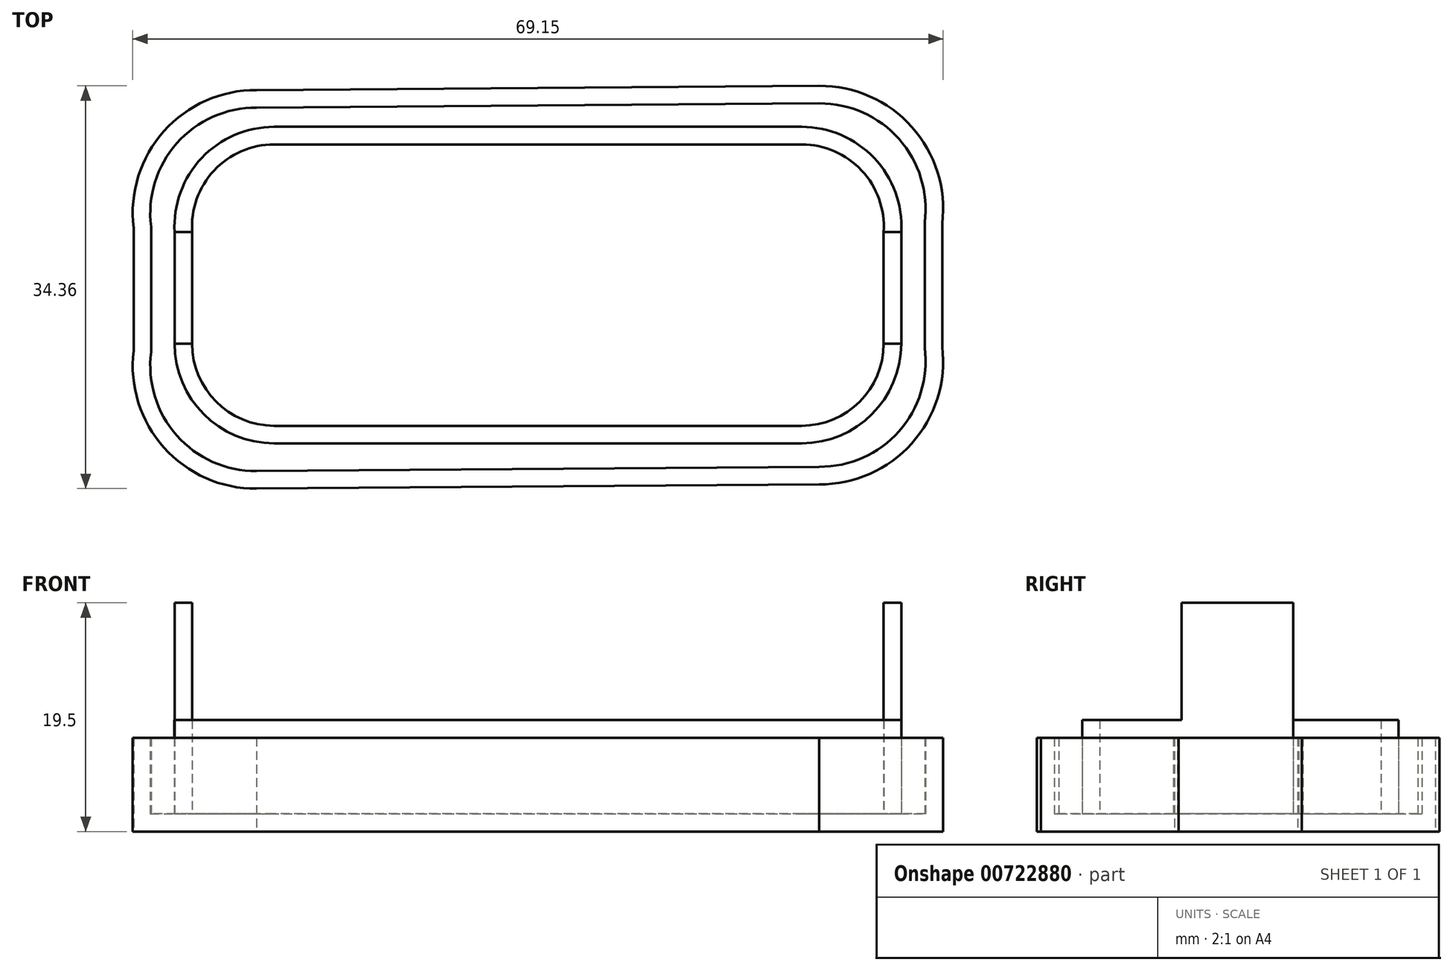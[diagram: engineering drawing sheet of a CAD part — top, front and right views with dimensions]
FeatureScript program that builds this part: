
annotation { "Feature Type Name" : "Feature", "Feature Type Description" : "" }
export const myFeature = defineFeature(function(context is Context, id is Id, definition is map)
    precondition{}
    {
        {
            var Q0;
            Q0=qCreatedBy(makeId("Top.planeOp"),FACE);
            var sketch = newSketch(context, id + "F0", { "sketchPlane" : qUnion([Q0])});
            skLineSegment(sketch, "E0.0", {"start": v(-24.12, -16.42) * mm, "end": v(23.88, -16.06) * mm});
            skArc(sketch, "E0.1", {"start": v(34.38, -4.31) * mm, "mid": v(31.79, -12.56) * mm, "end": v(23.88, -16.06) * mm});
            skLineSegment(sketch, "E0.2", {"start": v(34.38, 6.19) * mm, "end": v(34.38, -4.31) * mm});
            skArc(sketch, "E0.3", {"start": v(23.88, 17.94) * mm, "mid": v(31.79, 14.43) * mm, "end": v(34.38, 6.19) * mm});
            skLineSegment(sketch, "E0.4", {"start": v(-24.12, 17.58) * mm, "end": v(23.88, 17.94) * mm});
            skArc(sketch, "E0.5", {"start": v(-34.62, 5.83) * mm, "mid": v(-32.02, 14.07) * mm, "end": v(-24.12, 17.58) * mm});
            skLineSegment(sketch, "E0.6", {"start": v(-34.62, 5.83) * mm, "end": v(-34.62, -4.67) * mm});
            skArc(sketch, "E0.7", {"start": v(-24.12, -16.42) * mm, "mid": v(-32.02, -12.92) * mm, "end": v(-34.62, -4.67) * mm});
            skSolve(sketch);
        }
        {
            var Q0;
            Q0=qSketchRegion(id+"F0",true);
            extrude(context, id + "F1", {"entities" : qUnion([Q0]), "depth" : 8 * mm, "offsetDistance" : 25 * mm});
        }
        {
            var Q0;
            Q0=makeQuery(id+"F1.opExtrude","CAP_FACE",FACE,{"disambiguationData":[OSD([sQuery(id+"F0.wireOp",EDGE,"E0.0"),sQuery(id+"F0.wireOp",EDGE,"E0.1"),sQuery(id+"F0.wireOp",EDGE,"E0.2"),sQuery(id+"F0.wireOp",EDGE,"E0.3"),sQuery(id+"F0.wireOp",EDGE,"E0.4"),sQuery(id+"F0.wireOp",EDGE,"E0.5"),sQuery(id+"F0.wireOp",EDGE,"E0.6"),sQuery(id+"F0.wireOp",EDGE,"E0.7")])],"isStart":false});
            shell(context, id + "F2", {"entities" : qUnion([Q0]), "thickness" : 1.5 * mm});
        }
        {
            var Q0;
            Q0=makeQuery(id+"F2.opShell","OFFSET_FACE",FACE,{"disambiguationData":[OSD([sQuery(id+"F0.wireOp",EDGE,"E0.0"),sQuery(id+"F0.wireOp",EDGE,"E0.1"),sQuery(id+"F0.wireOp",EDGE,"E0.2"),sQuery(id+"F0.wireOp",EDGE,"E0.3"),sQuery(id+"F0.wireOp",EDGE,"E0.4"),sQuery(id+"F0.wireOp",EDGE,"E0.5"),sQuery(id+"F0.wireOp",EDGE,"E0.6"),sQuery(id+"F0.wireOp",EDGE,"E0.7")])]});
            var sketch = newSketch(context, id + "F3", { "sketchPlane" : qUnion([Q0])});
            skLineSegment(sketch, "E1.0", {"start": v(22.38, -12.56) * mm, "end": v(-22.62, -12.56) * mm});
            skArc(sketch, "E1.1", {"start": v(22.38, -12.56) * mm, "mid": v(28.4, -10.07) * mm, "end": v(30.88, -4.06) * mm});
            skLineSegment(sketch, "E1.2", {"start": v(30.88, -4.06) * mm, "end": v(30.88, 5.46) * mm});
            skArc(sketch, "E1.3", {"start": v(30.88, 5.46) * mm, "mid": v(28.57, 11.78) * mm, "end": v(22.4, 14.44) * mm});
            skLineSegment(sketch, "E1.4", {"start": v(22.4, 14.44) * mm, "end": v(-22.63, 14.44) * mm});
            skArc(sketch, "E1.5", {"start": v(-22.63, 14.44) * mm, "mid": v(-28.8, 11.78) * mm, "end": v(-31.12, 5.46) * mm});
            skLineSegment(sketch, "E1.6", {"start": v(-31.12, -4.06) * mm, "end": v(-31.12, 5.46) * mm});
            skArc(sketch, "E1.7", {"start": v(-31.12, -4.06) * mm, "mid": v(-28.63, -10.07) * mm, "end": v(-22.62, -12.56) * mm});
            skLineSegment(sketch, "E2", {"start": v(22.38, -11.06) * mm, "end": v(-22.62, -11.06) * mm});
            skLineSegment(sketch, "E3", {"start": v(22.4, 12.94) * mm, "end": v(-22.63, 12.94) * mm});
            skLineSegment(sketch, "E4", {"start": v(29.38, -4.06) * mm, "end": v(29.38, 5.46) * mm});
            skLineSegment(sketch, "E5", {"start": v(-29.62, 5.46) * mm, "end": v(-29.62, -4.06) * mm});
            skArc(sketch, "E6", {"start": v(22.38, -11.06) * mm, "mid": v(27.33, -9.01) * mm, "end": v(29.38, -4.06) * mm});
            skArc(sketch, "E7", {"start": v(29.38, 5.46) * mm, "mid": v(27.52, 10.72) * mm, "end": v(22.4, 12.94) * mm});
            skArc(sketch, "E8", {"start": v(-22.63, 12.94) * mm, "mid": v(-27.75, 10.72) * mm, "end": v(-29.62, 5.46) * mm});
            skArc(sketch, "E9", {"start": v(-29.62, -4.06) * mm, "mid": v(-27.57, -9.01) * mm, "end": v(-22.62, -11.06) * mm});
            skSolve(sketch);
        }
        {
            var Q0;
            Q0=qSketchRegion(id+"F3",true);
            extrude(context, id + "F4", {"entities" : qUnion([Q0]), "operationType" : NewBodyOperationType.ADD, "depth" : 18 * mm, "offsetDistance" : 25 * mm});
        }
        {
            var Q0;
            Q0=makeQuery(id+"F4.opExtrude","SWEPT_FACE",FACE,{"disambiguationData":[OSD([sQuery(id+"F3.wireOp",EDGE,"E1.2")])]});
            var sketch = newSketch(context, id + "F5", { "sketchPlane" : qUnion([Q0])});
            skLineSegment(sketch, "E10.bottom", {"start": v(-4.06, 9.5) * mm, "end": v(-19.06, 9.5) * mm});
            skLineSegment(sketch, "E10.top", {"start": v(-4.06, 19.5) * mm, "end": v(-19.06, 19.5) * mm});
            skLineSegment(sketch, "E10.left", {"start": v(-4.06, 9.5) * mm, "end": v(-4.06, 19.5) * mm});
            skLineSegment(sketch, "E10.right", {"start": v(-19.06, 9.5) * mm, "end": v(-19.06, 19.5) * mm});
            skSolve(sketch);
        }
        {
            var Q0;
            Q0=qSketchRegion(id+"F5",true);
            extrude(context, id + "F6", {"entities" : qUnion([Q0]), "operationType" : NewBodyOperationType.REMOVE, "endBound" : BoundingType.THROUGH_ALL, "oppositeDirection" : true, "depth" : 25 * mm, "offsetDistance" : 25 * mm});
        }
        {
            var Q0;
            Q0=makeQuery(id+"F4.opExtrude","CAP_FACE",FACE,{"disambiguationData":[OSD([sQuery(id+"F3.wireOp",EDGE,"E1.0"),sQuery(id+"F3.wireOp",EDGE,"E1.1"),sQuery(id+"F3.wireOp",EDGE,"E1.2"),sQuery(id+"F3.wireOp",EDGE,"E1.3"),sQuery(id+"F3.wireOp",EDGE,"E1.4"),sQuery(id+"F3.wireOp",EDGE,"E1.5"),sQuery(id+"F3.wireOp",EDGE,"E1.6"),sQuery(id+"F3.wireOp",EDGE,"E1.7"),sQuery(id+"F3.wireOp",EDGE,"E2"),sQuery(id+"F3.wireOp",EDGE,"E3"),sQuery(id+"F3.wireOp",EDGE,"E4"),sQuery(id+"F3.wireOp",EDGE,"E5"),sQuery(id+"F3.wireOp",EDGE,"E6"),sQuery(id+"F3.wireOp",EDGE,"E7"),sQuery(id+"F3.wireOp",EDGE,"E8"),sQuery(id+"F3.wireOp",EDGE,"E9")])],"isStart":false});
            var sketch = newSketch(context, id + "F7", { "sketchPlane" : qUnion([Q0])});
            skLineSegment(sketch, "E11.bottom", {"start": v(-37.63, 5.46) * mm, "end": v(35.77, 5.46) * mm});
            skLineSegment(sketch, "E11.top", {"start": v(-37.63, 19.9) * mm, "end": v(35.77, 19.9) * mm});
            skLineSegment(sketch, "E11.left", {"start": v(-37.63, 5.46) * mm, "end": v(-37.63, 19.9) * mm});
            skLineSegment(sketch, "E11.right", {"start": v(35.77, 5.46) * mm, "end": v(35.77, 19.9) * mm});
            skSolve(sketch);
        }
        {
            var Q0;
            Q0 = qSketchRegion(id + "F7", true);
            extrude(context, id + "F8", {"entities" : qUnion([Q0]), "operationType" : NewBodyOperationType.REMOVE, "oppositeDirection" : true, "depth" : 10 * mm, "offsetDistance" : 25 * mm});
        }
    });
